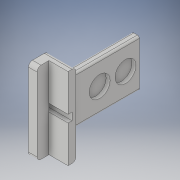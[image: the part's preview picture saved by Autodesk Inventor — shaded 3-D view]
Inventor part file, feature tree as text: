
AUTODESK INVENTOR PART (.ipt)
format: ipt  version: 2019 (Build 230136000, 136)  size: 301,056 bytes
history: native  units: in
note: dims shown in document units (in); Inventor stores cm internally (conversion verified against a paired STEP export)
features: reference x11, thicken_offset x10, sketch x7, extrude x7, fillet x2, projected_geometry x2, other x2, plane x1
ambient origin geometry x8: Origin, YZ Plane, XZ Plane, XY Plane, X Axis, Y Axis, Z Axis, Center Point
bodies: Solid1 (feature_tree)
feature tree (42):
  sketch  "Sketch2"  dims[d0=1.0in d1=0.0in d2=0.5906in d3=0.0in]
  plane  "Work Plane1"
  extrude  "Extrusion1"  Depth=0.5906in TaperAngle=0.0deg
  extrude  "Extrusion2"  Depth=1.8504in
  extrude  "Extrusion3"  Depth=0.2362in
  extrude  "Extrusion6"  Depth=0.0787in
  extrude  "Extrusion4"  Depth=0.0039in
  extrude  "Extrusion5"  Depth=0.0039in
  extrude  "Extrusion7"  Depth=0.0394in
  thicken_offset  "Thicken1"
  thicken_offset  "Thicken2"
  thicken_offset  "Thicken3"
  thicken_offset  "Thicken4"
  thicken_offset  "Thicken5"
  thicken_offset  "Thicken6"
  thicken_offset  "Thicken7"
  thicken_offset  "Thicken8"
  thicken_offset  "Thicken9"
  thicken_offset  "Thicken10"
  fillet  "Fillet2"  Radius=0.0039in
  fillet  "Fillet4"  Radius=0.0039in
  reference  "Reference1"
  reference  "Reference2"
  reference  "Reference3"
  reference  "Reference4"
  reference  "Reference5"
  reference  "Reference6"
  reference  "Reference7"
  reference  "Reference8"
  sketch  "Sketch3"  dims[d4=0.315in d5=1.8504in]
  projected_geometry  "Projected Loop1"
  sketch  "Sketch4"  dims[d6=0.2362in d7=0.0in d8=0.1496in]
  projected_geometry  "Projected Loop2"
  reference  "Reference9"
  sketch  "Sketch5"  dims[d9=0.0787in d10=0.0in d11=0.0039in]
  sketch  "Sketch6"  dims[d12=0.0039in d13=0.0039in]
  reference  "Reference10"
  reference  "Reference11"
  sketch  "Sketch7"  dims[d14=0.0039in d15=0.0039in]
  sketch  "Sketch9"  dims[d16=0.0039in d17=0.0039in d18=0.0039in d19=0.0039in d20=0.0039in d21=0.0039in d22=0.0039in d23=0.0039in d24=0.0039in d25=0.0039in d26=0.0039in d32=0.0827in d33=0.0in d34=1.6142in d35=0.7874in d36=0.1575in d37=0.0in d38=0.0079in d39=0.0157in d40=0.0079in d41=0.0079in d42=0.5512in d45=0.2362in d46=0.0in d47=0.0787in d48=0.0394in d49=0.1969in]
  parser-record x1  (decoder bookkeeping rows leaked as tree rows — omitted from the tree; the rows remain in map.json)
  other  "zplate_assembly.iam"
note: 1 file-system path scrubbed to <path> (originals preserved in map.json)
